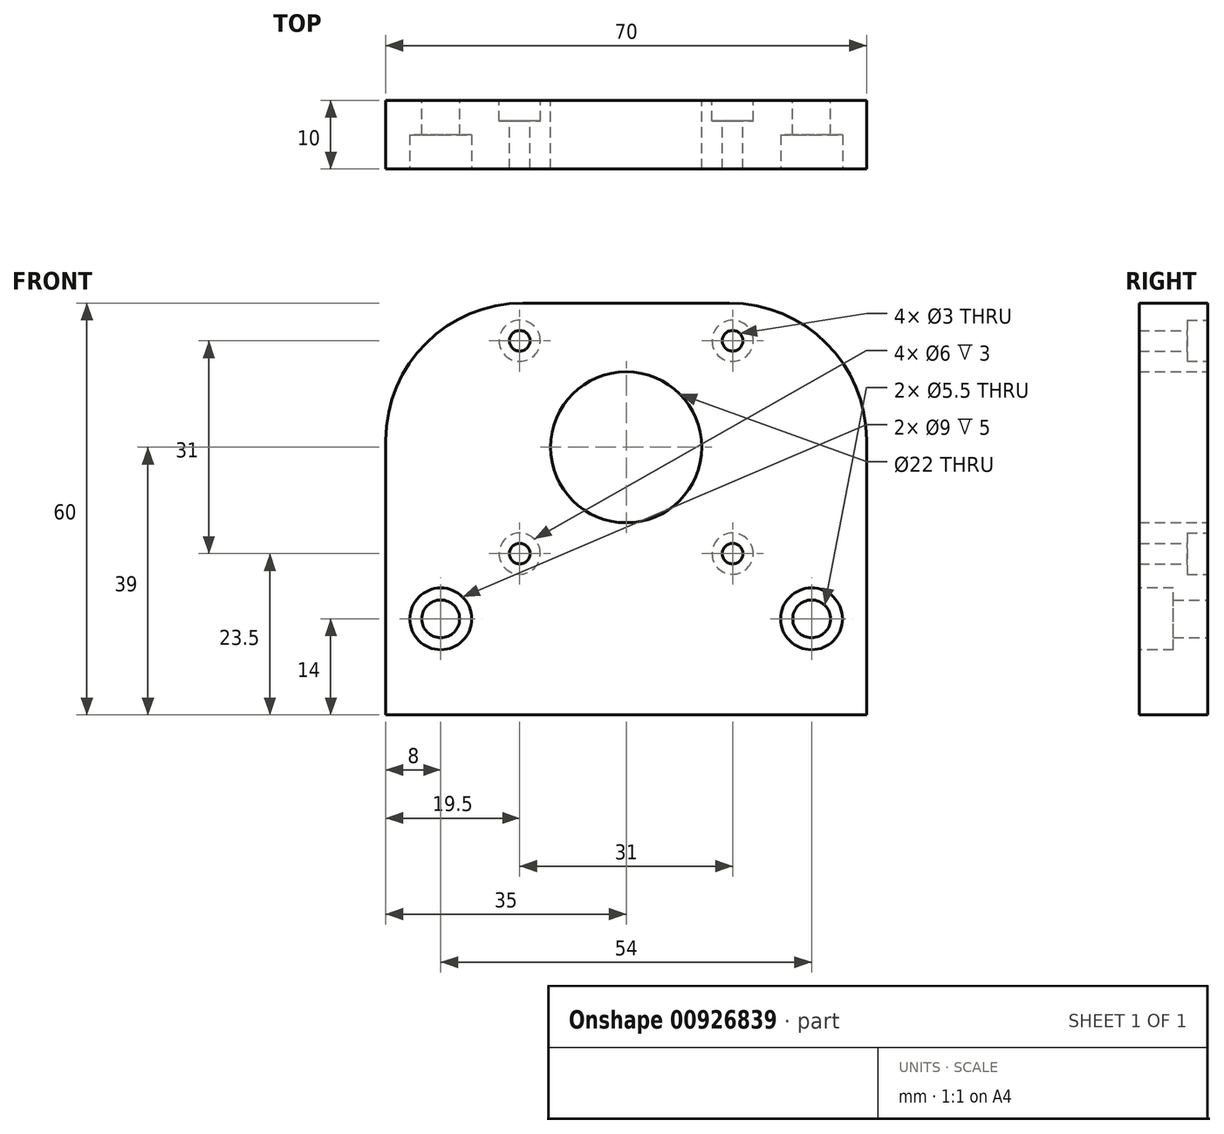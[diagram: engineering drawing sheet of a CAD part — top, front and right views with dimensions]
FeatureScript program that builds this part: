
annotation { "Feature Type Name" : "Feature", "Feature Type Description" : "" }
export const myFeature = defineFeature(function(context is Context, id is Id, definition is map)
    precondition{}
    {
        {
            var Q0;
            Q0=qCreatedBy(makeId("Front.planeOp"),FACE);
            var sketch = newSketch(context, id + "F0", { "sketchPlane" : qUnion([Q0])});
            skLineSegment(sketch, "E0.bottom", {"start": v(0, 60) * mm, "end": v(70, 60) * mm});
            skLineSegment(sketch, "E0.top", {"start": v(0, 0) * mm, "end": v(70, 0) * mm});
            skLineSegment(sketch, "E0.left", {"start": v(0, 60) * mm, "end": v(0, 0) * mm});
            skLineSegment(sketch, "E0.right", {"start": v(70, 60) * mm, "end": v(70, 0) * mm});
            skLineSegment(sketch, "E1", {"start": v(35, 60) * mm, "end": v(35, 0) * mm, "construction": true});
            skCircle(sketch, "E2", {"center": v(35, 39) * mm, "radius": 11 * mm});
            skCircle(sketch, "E3", {"center": v(50.5, 54.5) * mm, "radius": 1.5 * mm});
            skLineSegment(sketch, "E4", {"start": v(50.5, 54.5) * mm, "end": v(35, 39) * mm, "construction": true});
            skCircle(sketch, "E5.1.0", {"center": v(19.5, 54.5) * mm, "radius": 1.5 * mm});
            skCircle(sketch, "E5.2.0", {"center": v(19.5, 23.5) * mm, "radius": 1.5 * mm});
            skCircle(sketch, "E5.3.0", {"center": v(50.5, 23.5) * mm, "radius": 1.5 * mm});
            skLineSegment(sketch, "E6", {"start": v(35, 39) * mm, "end": v(70, 39) * mm, "construction": true});
            skLineSegment(sketch, "E7", {"start": v(35, 84.75) * mm, "end": v(70, 84.75) * mm, "construction": true});
            skLineSegment(sketch, "E8", {"start": v(35, 14) * mm, "end": v(70, 14) * mm, "construction": true});
            skCircle(sketch, "E9", {"center": v(62, 14) * mm, "radius": 2.75 * mm});
            skLineSegment(sketch, "E10.bottom", {"start": v(56.5, 17.5) * mm, "end": v(13.5, 17.5) * mm, "construction": true});
            skLineSegment(sketch, "E10.top", {"start": v(56.5, 60.5) * mm, "end": v(13.5, 60.5) * mm, "construction": true});
            skLineSegment(sketch, "E10.left", {"start": v(56.5, 17.5) * mm, "end": v(56.5, 60.5) * mm, "construction": true});
            skLineSegment(sketch, "E10.right", {"start": v(13.5, 17.5) * mm, "end": v(13.5, 60.5) * mm, "construction": true});
            skCircle(sketch, "E11", {"center": v(8, 14) * mm, "radius": 2.75 * mm});
            skLineSegment(sketch, "E12", {"start": v(35, 14) * mm, "end": v(0, 14) * mm, "construction": true});
            skSolve(sketch);
        }
        {
            var Q0;
            Q0 = qSketchRegion(id + "F0", true);
            extrude(context, id + "F1", {"entities" : qUnion([Q0]), "depth" : 10 * mm, "offsetDistance" : 25 * mm});
        }
        {
            var Q0;
            Q0=makeQuery(id+"F1.opExtrude","CAP_FACE",FACE,{"disambiguationData":[OSD([sQuery(id+"F0.wireOp",EDGE,"E0.bottom"),sQuery(id+"F0.wireOp",EDGE,"E0.top"),sQuery(id+"F0.wireOp",EDGE,"E0.left"),sQuery(id+"F0.wireOp",EDGE,"E0.right")])],"isStart":false});
            var sketch = newSketch(context, id + "F2", { "sketchPlane" : qUnion([Q0])});
            skCircle(sketch, "E13", {"center": v(8, 14) * mm, "radius": 4.5 * mm});
            skCircle(sketch, "E14", {"center": v(62, 14) * mm, "radius": 4.5 * mm});
            skSolve(sketch);
        }
        {
            var Q0;
            Q0=makeQuery(id+"F1.opExtrude","SWEPT_EDGE",EDGE,{"disambiguationData":[OSD([sQuery(id+"F0.wireOp",EDGE,"E0.bottom"),sQuery(id+"F0.wireOp",EDGE,"E0.right")])]});
            var Q1;
            Q1=makeQuery(id+"F1.opExtrude","SWEPT_EDGE",EDGE,{"disambiguationData":[OSD([sQuery(id+"F0.wireOp",EDGE,"E0.bottom"),sQuery(id+"F0.wireOp",EDGE,"E0.left")])]});
            fillet(context, id + "F3", {"entities" : qUnion([Q0, Q1]), "radius" : 20 * mm, "tangentPropagation" : true, "defaultsChanged" : false, "vertexSettings" : [], "allowEdgeOverflow" : false});
        }
        {
            var Q0;
            Q0=makeQuery(id+"F2.imprint","IMPRINT",FACE,{"disambiguationData":[TD([[makeQuery(id+"F2.imprint","IMPRINT",EDGE,{"derivedFrom":sQuery(id+"F2.wireOp",EDGE,"E13")}),1.0]])]});
            var Q1;
            Q1=makeQuery(id+"F2.imprint","IMPRINT",FACE,{"disambiguationData":[TD([[makeQuery(id+"F2.imprint","IMPRINT",EDGE,{"derivedFrom":sQuery(id+"F2.wireOp",EDGE,"E14")}),1.0]])]});
            extrude(context, id + "F4", {"entities" : qUnion([Q0, Q1]), "operationType" : NewBodyOperationType.REMOVE, "oppositeDirection" : true, "depth" : 5 * mm, "offsetDistance" : 25 * mm});
        }
        {
            var Q0;
            Q0=makeQuery(id+"F1.opExtrude","CAP_FACE",FACE,{"disambiguationData":[OSD([sQuery(id+"F0.wireOp",EDGE,"E0.bottom"),sQuery(id+"F0.wireOp",EDGE,"E0.top"),sQuery(id+"F0.wireOp",EDGE,"E0.left"),sQuery(id+"F0.wireOp",EDGE,"E0.right"),sQuery(id+"F0.wireOp",EDGE,"E2"),sQuery(id+"F0.wireOp",EDGE,"E3"),sQuery(id+"F0.wireOp",EDGE,"E5.1.0"),sQuery(id+"F0.wireOp",EDGE,"E5.2.0"),sQuery(id+"F0.wireOp",EDGE,"E5.3.0"),sQuery(id+"F0.wireOp",EDGE,"E9"),sQuery(id+"F0.wireOp",EDGE,"E11")])],"isStart":true});
            var sketch = newSketch(context, id + "F5", { "sketchPlane" : qUnion([Q0])});
            skCircle(sketch, "E15", {"center": v(-50.5, 54.5) * mm, "radius": 3 * mm});
            skCircle(sketch, "E16", {"center": v(-19.5, 54.5) * mm, "radius": 3 * mm});
            skCircle(sketch, "E17", {"center": v(-19.5, 23.5) * mm, "radius": 3 * mm});
            skCircle(sketch, "E18", {"center": v(-50.5, 23.5) * mm, "radius": 3 * mm});
            skSolve(sketch);
        }
        {
            var Q0;
            Q0=makeQuery(id+"F5.imprint","IMPRINT",FACE,{"disambiguationData":[TD([[makeQuery(id+"F5.imprint","IMPRINT",EDGE,{"derivedFrom":sQuery(id+"F5.wireOp",EDGE,"E15")}),1.0]])]});
            var Q1;
            Q1=makeQuery(id+"F5.imprint","IMPRINT",FACE,{"disambiguationData":[TD([[makeQuery(id+"F5.imprint","IMPRINT",EDGE,{"derivedFrom":sQuery(id+"F5.wireOp",EDGE,"E16")}),1.0]])]});
            var Q2;
            Q2=makeQuery(id+"F5.imprint","IMPRINT",FACE,{"disambiguationData":[TD([[makeQuery(id+"F5.imprint","IMPRINT",EDGE,{"derivedFrom":sQuery(id+"F5.wireOp",EDGE,"E17")}),1.0]])]});
            var Q3;
            Q3=makeQuery(id+"F5.imprint","IMPRINT",FACE,{"disambiguationData":[TD([[makeQuery(id+"F5.imprint","IMPRINT",EDGE,{"derivedFrom":sQuery(id+"F5.wireOp",EDGE,"E18")}),1.0]])]});
            extrude(context, id + "F6", {"entities" : qUnion([Q0, Q1, Q2, Q3]), "operationType" : NewBodyOperationType.REMOVE, "oppositeDirection" : true, "depth" : 3 * mm, "offsetDistance" : 25 * mm});
        }
    });
